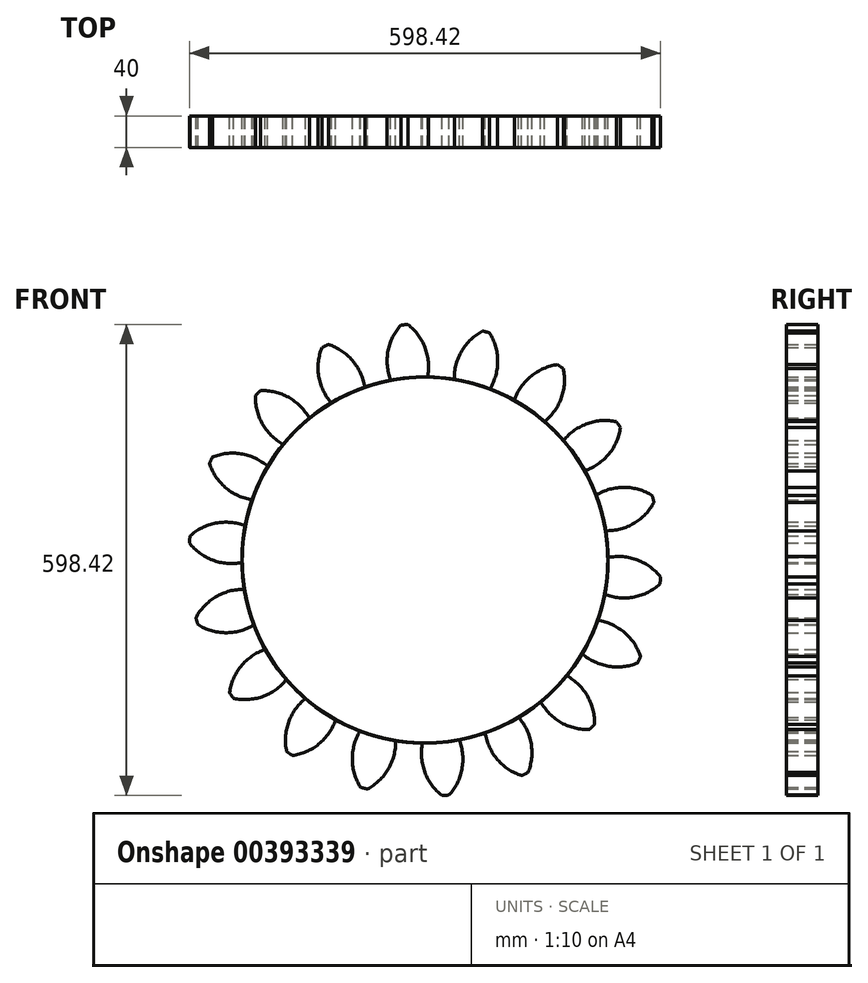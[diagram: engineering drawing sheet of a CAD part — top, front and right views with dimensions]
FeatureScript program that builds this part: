
annotation { "Feature Type Name" : "Feature", "Feature Type Description" : "" }
export const myFeature = defineFeature(function(context is Context, id is Id, definition is map)
    precondition{}
    {
        {
            var Q0;
            Q0=qCreatedBy(makeId("Front.planeOp"),FACE);
            var sketch = newSketch(context, id + "F0", { "sketchPlane" : qUnion([Q0])});
            skCircle(sketch, "E0", {"center": v(0, 0) * mm, "radius": 300 * mm, "construction": true});
            skCircle(sketch, "E1", {"center": v(0, 0) * mm, "radius": 270 * mm, "construction": true});
            skCircle(sketch, "E2", {"center": v(0, 0) * mm, "radius": 253.72 * mm, "construction": true});
            skLineSegment(sketch, "E3", {"start": v(0, 0) * mm, "end": v(0, 349.16) * mm, "construction": true});
            skLineSegment(sketch, "E4", {"start": v(0, 0) * mm, "end": v(-30.46, 348.11) * mm, "construction": true});
            skLineSegment(sketch, "E5", {"start": v(0, 270) * mm, "end": v(-226.89, 270) * mm, "construction": true});
            skLineSegment(sketch, "E6", {"start": v(0, 270) * mm, "end": v(-291.33, 163.96) * mm, "construction": true});
            skCircle(sketch, "E7", {"center": v(0, 270) * mm, "radius": 67.5 * mm, "construction": true});
            skCircle(sketch, "E8", {"center": v(0, 0) * mm, "radius": 232.5 * mm});
            skCircle(sketch, "E9", {"center": v(-62.95, 245.78) * mm, "radius": 67.5 * mm, "construction": true});
            skArc(sketch, "E10", {"start": v(0, 270) * mm, "mid": v(-8.83, 286.1) * mm, "end": v(-21.7, 299.21) * mm});
            skArc(sketch, "E11", {"start": v(3.23, 232.48) * mm, "mid": v(4.24, 251.46) * mm, "end": v(0, 270) * mm});
            skArc(sketch, "E12.MirrorCS", {"start": v(-46.89, 265.9) * mm, "mid": v(-40.99, 283.3) * mm, "end": v(-30.59, 298.44) * mm});
            skArc(sketch, "E13.MirrorCS", {"start": v(-43.55, 228.39) * mm, "mid": v(-47.84, 246.9) * mm, "end": v(-46.89, 265.9) * mm});
            skArc(sketch, "E14", {"start": v(-21.7, 299.21) * mm, "mid": v(-26.15, 298.9) * mm, "end": v(-30.59, 298.44) * mm});
            skSolve(sketch);
        }
        {
            var Q0;
            {var subQ0=sQuery(id+"F0.wireOp",EDGE,"E8");var subQ1=makeQuery(id+"F0.imprint","INTERSECT",VERTEX,{"derivedFrom":[subQ0,sQuery(id+"F0.wireOp",EDGE,"E11")]});Q0=makeQuery(id+"F0.imprint","IMPRINT",FACE,{"disambiguationData":[TD([[makeQuery(id+"F0.imprint","IMPRINT",EDGE,{"disambiguationData":[TD([[subQ1,-1.0]])],"derivedFrom":subQ0}),1.0]])]});}
            var Q1;
            Q1=makeQuery(id+"F0.imprint","IMPRINT",FACE,{"disambiguationData":[TD([[makeQuery(id+"F0.imprint","IMPRINT",EDGE,{"derivedFrom":sQuery(id+"F0.wireOp",EDGE,"E10")}),1.0]])]});
            extrude(context, id + "F1", {"entities" : qUnion([Q0, Q1]), "depth" : 40 * mm});
        }
        {
            var Q0;
            Q0=makeQuery(id+"F1.opExtrude","SWEPT_BODY",BODY,{"disambiguationData":[OSD([sQuery(id+"F0.wireOp",EDGE,"E8"),sQuery(id+"F0.wireOp",EDGE,"E10"),sQuery(id+"F0.wireOp",EDGE,"E11"),sQuery(id+"F0.wireOp",EDGE,"E12.MirrorCS"),sQuery(id+"F0.wireOp",EDGE,"E13.MirrorCS"),sQuery(id+"F0.wireOp",EDGE,"E14")])]});
            var Q1;
            Q1=makeQuery(id+"F1.opExtrude","SWEPT_FACE",FACE,{"disambiguationData":[OSD([sQuery(id+"F0.wireOp",EDGE,"E8")])]});
            circularPattern(context, id + "F2", {"entities" : qUnion([Q0]), "axis" : qUnion([Q1]), "angle" : 20 * degree, "instanceCount" : 18});
        }
    });
